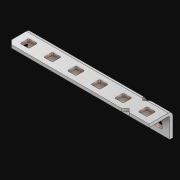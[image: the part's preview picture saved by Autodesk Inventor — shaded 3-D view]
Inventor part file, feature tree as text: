
AUTODESK INVENTOR PART (.ipt)
format: ipt  version: 2021 (Build 250183000, 183)  size: 582,144 bytes
history: native  units: in
note: dims shown in document units (in); Inventor stores cm internally (conversion verified against a paired STEP export)
features: extrude x13, other x12, sketch x3, pattern_linear x1, sheet_metal_op x1
ambient origin geometry x8: Origin, YZ Plane, XZ Plane, XY Plane, X Axis, Y Axis, Z Axis, Center Point
bodies: Solid1 (feature_tree)
feature tree (30):
  pattern_linear  "Rectangular Pattern1"  Spacing1=0.063in  [1 undecoded]
  extrude  "Extrusion1"  Depth=0.5in
  sketch  "Sketch1"  dims[d0=0.182in]
  other  "Srf1"
  sketch  "Sketch2"  dims[d1=0.063in d2=0.0in]
  other  "Srf2"
  other  "Srf3"
  other  "Srf5"
  other  "Srf7"
  other  "Srf9"
  other  "Srf11"
  other  "Srf4"
  other  "Srf6"
  other  "Srf8"
  other  "Srf10"
  other  "Srf12"
  sketch  "Sketch3"  dims[d3=0.182in d4=0.063in d5=0.0in d8=0.5in d9=14.5in d10=0.0in]
  sheet_metal_op  "Fold1"
  extrude  "ExtrusionSrf1"  Depth=0.5in TaperAngle=0.0deg
  extrude  "ExtrusionSrf2"  [1 undecoded]
  extrude  "ExtrusionSrf3"  [1 undecoded]
  extrude  "ExtrusionSrf4"  [1 undecoded]
  extrude  "ExtrusionSrf5"  [1 undecoded]
  extrude  "ExtrusionSrf6"  [1 undecoded]
  extrude  "ExtrusionSrf7"  [1 undecoded]
  extrude  "ExtrusionSrf37"  [1 undecoded]
  extrude  "ExtrusionSrf38"  [1 undecoded]
  extrude  "ExtrusionSrf39"  [1 undecoded]
  extrude  "ExtrusionSrf40"  [1 undecoded]
  extrude  "ExtrusionSrf41"  [1 undecoded]
note: 12 required parameter values undecoded (feature->parameter linkage not recoverable at this tier; creation-order binding heuristic only, values carry confidence <= 0.55)
